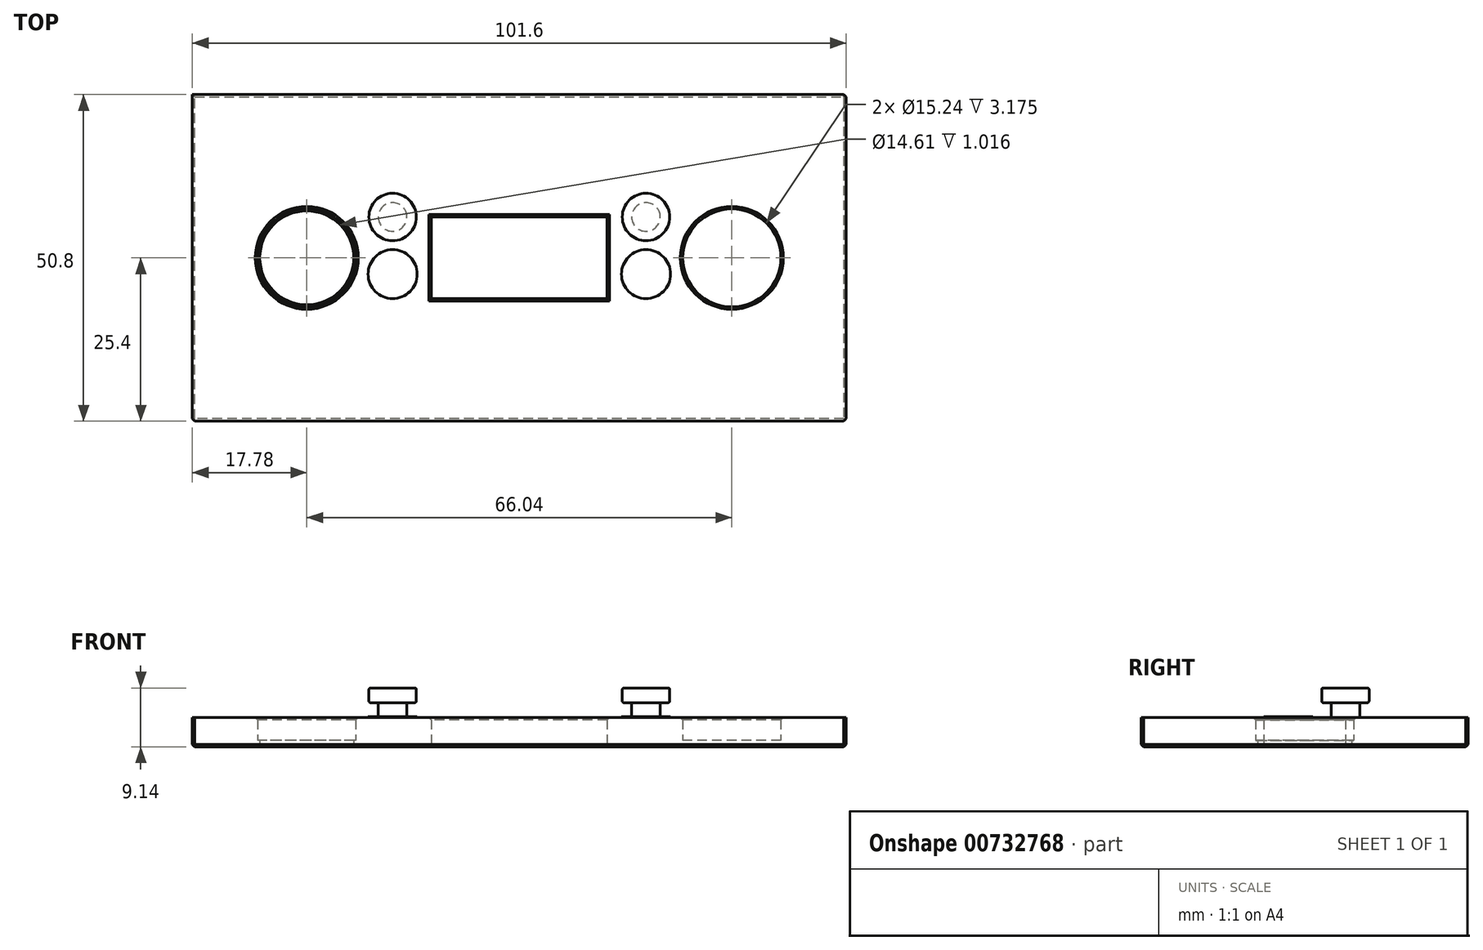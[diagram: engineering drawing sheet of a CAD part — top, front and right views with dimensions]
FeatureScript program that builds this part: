
annotation { "Feature Type Name" : "Feature", "Feature Type Description" : "" }
export const myFeature = defineFeature(function(context is Context, id is Id, definition is map)
    precondition{}
    {
        {
            var Q0;
            Q0=qCreatedBy(makeId("Top.planeOp"),FACE);
            var sketch = newSketch(context, id + "F0", { "sketchPlane" : qUnion([Q0])});
            skLineSegment(sketch, "E0.bottom", {"start": v(-50.8, 25.4) * mm, "end": v(50.8, 25.4) * mm});
            skLineSegment(sketch, "E0.top", {"start": v(-50.8, -25.4) * mm, "end": v(50.8, -25.4) * mm});
            skLineSegment(sketch, "E0.left", {"start": v(-50.8, 25.4) * mm, "end": v(-50.8, -25.4) * mm});
            skLineSegment(sketch, "E0.right", {"start": v(50.8, 25.4) * mm, "end": v(50.8, -25.4) * mm});
            skPoint(sketch, "E0.middle", {"position": v(0, 0) * mm});
            skLineSegment(sketch, "E1.bottom", {"start": v(-13.65, 6.35) * mm, "end": v(13.65, 6.35) * mm});
            skLineSegment(sketch, "E1.top", {"start": v(-13.65, -6.35) * mm, "end": v(13.65, -6.35) * mm});
            skLineSegment(sketch, "E1.left", {"start": v(-13.65, 6.35) * mm, "end": v(-13.65, -6.35) * mm});
            skLineSegment(sketch, "E1.right", {"start": v(13.65, 6.35) * mm, "end": v(13.65, -6.35) * mm});
            skCircle(sketch, "E2", {"center": v(-33.02, 0) * mm, "radius": 7.62 * mm});
            skCircle(sketch, "E3", {"center": v(33.02, 0) * mm, "radius": 7.62 * mm});
            skCircle(sketch, "E4", {"center": v(-19.68, -2.54) * mm, "radius": 3.81 * mm});
            skCircle(sketch, "E5", {"center": v(-19.68, 6.35) * mm, "radius": 2.22 * mm});
            skCircle(sketch, "E6", {"center": v(19.69, -2.54) * mm, "radius": 3.81 * mm});
            skCircle(sketch, "E7", {"center": v(19.69, 6.35) * mm, "radius": 2.22 * mm});
            skCircle(sketch, "E8", {"center": v(-33.02, 0) * mm, "radius": 7.3 * mm});
            skSolve(sketch);
        }
        {
            var Q0;
            Q0=makeQuery(id+"F0.imprint","IMPRINT",FACE,{"disambiguationData":[TD([[makeQuery(id+"F0.imprint","IMPRINT",EDGE,{"derivedFrom":sQuery(id+"F0.wireOp",EDGE,"E0.bottom")}),-1.0]])]});
            extrude(context, id + "F1", {"entities" : qUnion([Q0]), "depth" : 4.57 * mm, "offsetDistance" : 25.4 * mm});
        }
        {
            var Q0;
            Q0 = qSketchRegion(id + "F0", true);
            var Q1;
            Q1=makeQuery(id+"F0.imprint","IMPRINT",FACE,{"disambiguationData":[TD([[makeQuery(id+"F0.imprint","IMPRINT",EDGE,{"derivedFrom":sQuery(id+"F0.wireOp",EDGE,"E3")}),1.0]])]});
            var Q2;
            Q2=makeQuery(id+"F0.imprint","IMPRINT",FACE,{"disambiguationData":[TD([[makeQuery(id+"F0.imprint","IMPRINT",EDGE,{"derivedFrom":sQuery(id+"F0.wireOp",EDGE,"E2")}),1.0]])]});
            extrude(context, id + "F2", {"entities" : qUnion([Q0, Q1, Q2]), "operationType" : NewBodyOperationType.ADD, "depth" : 1.02 * mm, "offsetDistance" : 25.4 * mm});
        }
        {
            var Q0;
            Q0=makeQuery(id+"F0.imprint","IMPRINT",FACE,{"disambiguationData":[TD([[makeQuery(id+"F0.imprint","IMPRINT",EDGE,{"derivedFrom":sQuery(id+"F0.wireOp",EDGE,"E7")}),1.0]])]});
            var Q1;
            Q1=makeQuery(id+"F0.imprint","IMPRINT",FACE,{"disambiguationData":[TD([[makeQuery(id+"F0.imprint","IMPRINT",EDGE,{"derivedFrom":sQuery(id+"F0.wireOp",EDGE,"E7")}),1.0]])]});
            var Q2;
            Q2=makeQuery(id+"F0.imprint","IMPRINT",FACE,{"disambiguationData":[TD([[makeQuery(id+"F0.imprint","IMPRINT",EDGE,{"derivedFrom":sQuery(id+"F0.wireOp",EDGE,"E5")}),1.0]])]});
            extrude(context, id + "F3", {"entities" : qUnion([Q0, Q1, Q2]), "operationType" : NewBodyOperationType.ADD, "depth" : 6.86 * mm, "offsetDistance" : 25.4 * mm});
        }
        {
            var Q0;
            Q0=makeQuery(id+"F0.imprint","IMPRINT",FACE,{"disambiguationData":[TD([[makeQuery(id+"F0.imprint","IMPRINT",EDGE,{"derivedFrom":sQuery(id+"F0.wireOp",EDGE,"E4")}),1.0]])]});
            var Q1;
            Q1=makeQuery(id+"F0.imprint","IMPRINT",FACE,{"disambiguationData":[TD([[makeQuery(id+"F0.imprint","IMPRINT",EDGE,{"derivedFrom":sQuery(id+"F0.wireOp",EDGE,"E6")}),1.0]])]});
            extrude(context, id + "F4", {"entities" : qUnion([Q0, Q1]), "operationType" : NewBodyOperationType.ADD, "depth" : 4.67 * mm, "offsetDistance" : 25.4 * mm});
        }
        {
            var Q0;
            Q0=makeQuery(id+"F3.opExtrude","CAP_FACE",FACE,{"disambiguationData":[OSD([sQuery(id+"F0.wireOp",EDGE,"E7")])],"isStart":false});
            var sketch = newSketch(context, id + "F5", { "sketchPlane" : qUnion([Q0])});
            skCircle(sketch, "E9", {"center": v(-19.68, 6.35) * mm, "radius": 3.68 * mm});
            skCircle(sketch, "E10", {"center": v(19.69, 6.35) * mm, "radius": 3.68 * mm});
            skSolve(sketch);
        }
        {
            var Q0;
            Q0=makeQuery(id+"F5.imprint","IMPRINT",FACE,{"disambiguationData":[TD([[makeQuery(id+"F5.imprint","IMPRINT",EDGE,{"derivedFrom":sQuery(id+"F5.wireOp",EDGE,"E9")}),1.0]])]});
            var Q1;
            Q1=makeQuery(id+"F5.imprint","IMPRINT",FACE,{"disambiguationData":[TD([[makeQuery(id+"F5.imprint","IMPRINT",EDGE,{"derivedFrom":makeQuery(id+"F3.opExtrude","CAP_EDGE",EDGE,{"disambiguationData":[OSD([sQuery(id+"F0.wireOp",EDGE,"E7")])],"isStart":false})}),1.0]])]});
            var Q2;
            Q2=makeQuery(id+"F5.imprint","IMPRINT",FACE,{"disambiguationData":[TD([[makeQuery(id+"F5.imprint","IMPRINT",EDGE,{"derivedFrom":sQuery(id+"F5.wireOp",EDGE,"E10")}),1.0]])]});
            extrude(context, id + "F6", {"entities" : qUnion([Q0, Q1, Q2]), "operationType" : NewBodyOperationType.ADD, "depth" : 2.3 * mm, "offsetDistance" : 25.4 * mm});
        }
        {
            var Q0;
            Q0=makeQuery(id+"F6.opExtrude","CAP_EDGE",EDGE,{"disambiguationData":[OSD([sQuery(id+"F5.wireOp",EDGE,"E9")])],"isStart":false});
            var Q1;
            Q1=makeQuery(id+"F6.opExtrude","SWEPT_FACE",FACE,{"disambiguationData":[OSD([sQuery(id+"F5.wireOp",EDGE,"E9")])]});
            var Q2;
            Q2=makeQuery(id+"F6.opExtrude","CAP_EDGE",EDGE,{"disambiguationData":[OSD([sQuery(id+"F5.wireOp",EDGE,"E10")])],"isStart":false});
            var Q3;
            Q3=makeQuery(id+"F6.opExtrude","CAP_EDGE",EDGE,{"disambiguationData":[OSD([sQuery(id+"F5.wireOp",EDGE,"E10")])],"isStart":true});
            fillet(context, id + "F7", {"entities" : qUnion([Q0, Q1, Q2, Q3]), "radius" : 0.25 * mm, "tangentPropagation" : true, "allowEdgeOverflow" : false});
        }
        {
            var Q0;
            Q0=makeQuery(id+"F1.opExtrude","CAP_EDGE",EDGE,{"disambiguationData":[OSD([sQuery(id+"F0.wireOp",EDGE,"E3")])],"isStart":false});
            var Q1;
            Q1=makeQuery(id+"F1.opExtrude","CAP_EDGE",EDGE,{"disambiguationData":[OSD([sQuery(id+"F0.wireOp",EDGE,"E2")])],"isStart":false});
            var Q2;
            Q2=makeQuery(id+"F1.opExtrude","SWEPT_EDGE",EDGE,{"disambiguationData":[OSD([sQuery(id+"F0.wireOp",EDGE,"E0.bottom"),sQuery(id+"F0.wireOp",EDGE,"E0.right")])]});
            var Q3;
            Q3=makeQuery(id+"F1.opExtrude","CAP_EDGE",EDGE,{"disambiguationData":[OSD([sQuery(id+"F0.wireOp",EDGE,"E0.bottom")])],"isStart":true});
            var Q4;
            Q4=makeQuery(id+"F1.opExtrude","CAP_EDGE",EDGE,{"disambiguationData":[OSD([sQuery(id+"F0.wireOp",EDGE,"E0.right")])],"isStart":true});
            var Q5;
            Q5=makeQuery(id+"F1.opExtrude","SWEPT_EDGE",EDGE,{"disambiguationData":[OSD([sQuery(id+"F0.wireOp",EDGE,"E0.top"),sQuery(id+"F0.wireOp",EDGE,"E0.right")])]});
            var Q6;
            Q6=makeQuery(id+"F1.opExtrude","CAP_EDGE",EDGE,{"disambiguationData":[OSD([sQuery(id+"F0.wireOp",EDGE,"E0.top")])],"isStart":true});
            var Q7;
            Q7=makeQuery(id+"F1.opExtrude","SWEPT_EDGE",EDGE,{"disambiguationData":[OSD([sQuery(id+"F0.wireOp",EDGE,"E0.top"),sQuery(id+"F0.wireOp",EDGE,"E0.left")])]});
            var Q8;
            Q8=makeQuery(id+"F1.opExtrude","CAP_EDGE",EDGE,{"disambiguationData":[OSD([sQuery(id+"F0.wireOp",EDGE,"E0.left")])],"isStart":true});
            var Q9;
            Q9=makeQuery(id+"F1.opExtrude","CAP_EDGE",EDGE,{"disambiguationData":[OSD([sQuery(id+"F0.wireOp",EDGE,"E1.bottom")])],"isStart":false});
            var Q10;
            Q10=makeQuery(id+"F1.opExtrude","CAP_EDGE",EDGE,{"disambiguationData":[OSD([sQuery(id+"F0.wireOp",EDGE,"E1.left")])],"isStart":false});
            var Q11;
            Q11=makeQuery(id+"F1.opExtrude","CAP_EDGE",EDGE,{"disambiguationData":[OSD([sQuery(id+"F0.wireOp",EDGE,"E1.top")])],"isStart":false});
            var Q12;
            Q12=makeQuery(id+"F1.opExtrude","CAP_EDGE",EDGE,{"disambiguationData":[OSD([sQuery(id+"F0.wireOp",EDGE,"E1.right")])],"isStart":false});
            chamfer(context, id + "F8", {"entities" : qUnion([Q0, Q1, Q2, Q3, Q4, Q5, Q6, Q7, Q8, Q9, Q10, Q11, Q12]), "width" : 0.38 * mm, "tangentPropagation" : true});
        }
    });
